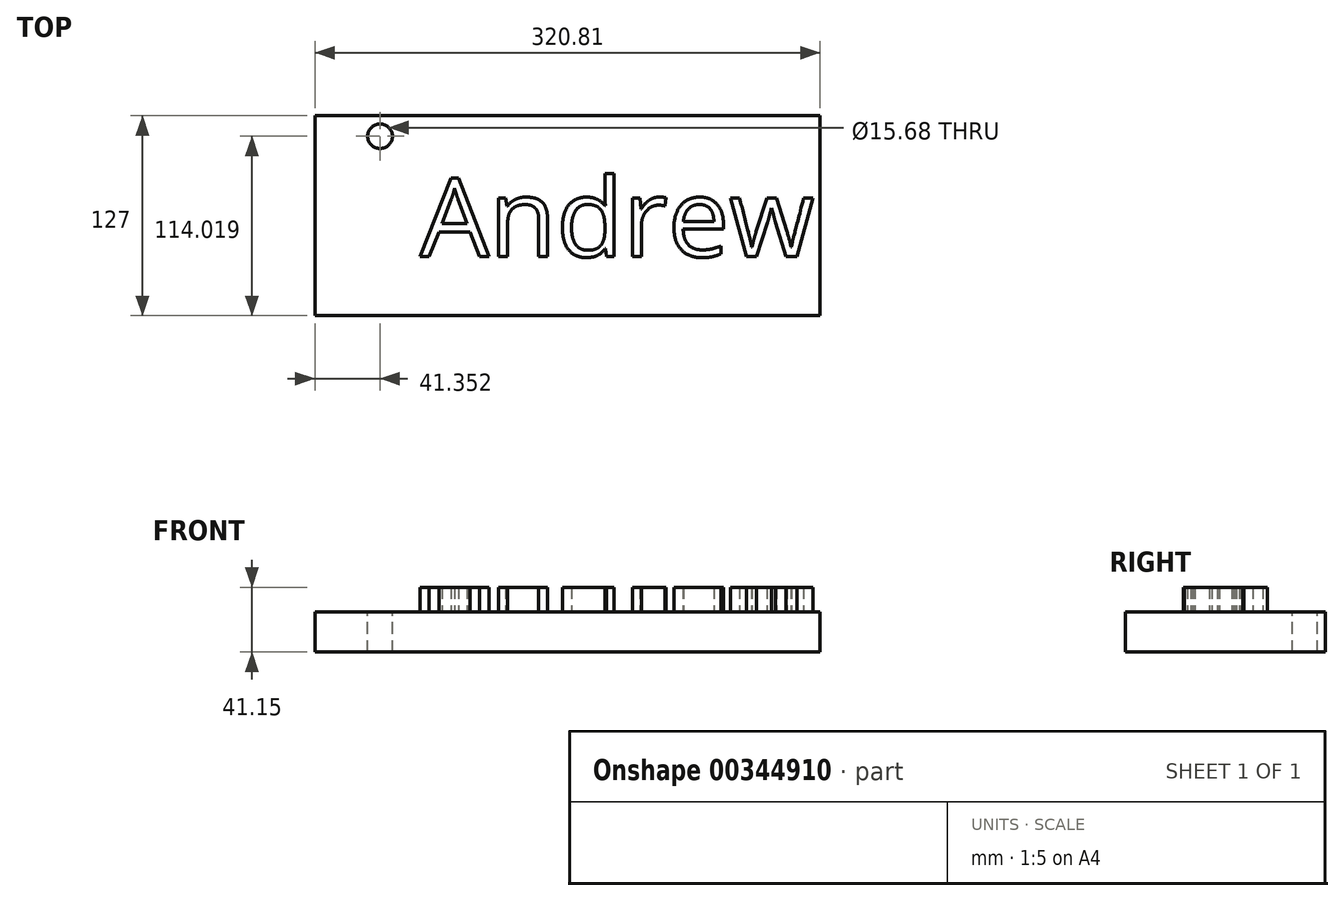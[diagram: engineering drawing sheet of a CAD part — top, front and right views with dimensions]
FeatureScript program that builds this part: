
annotation { "Feature Type Name" : "Feature", "Feature Type Description" : "" }
export const myFeature = defineFeature(function(context is Context, id is Id, definition is map)
    precondition{}
    {
        {
            var Q0;
            Q0=qCreatedBy(makeId("Top.planeOp"),FACE);
            var sketch = newSketch(context, id + "F0", { "sketchPlane" : qUnion([Q0])});
            skLineSegment(sketch, "E0.bottom", {"start": v(-187.13, 76.34) * mm, "end": v(133.68, 76.34) * mm});
            skLineSegment(sketch, "E0.top", {"start": v(-187.13, -50.66) * mm, "end": v(133.68, -50.66) * mm});
            skLineSegment(sketch, "E0.left", {"start": v(-187.13, 76.34) * mm, "end": v(-187.13, -50.66) * mm});
            skLineSegment(sketch, "E0.right", {"start": v(133.68, 76.34) * mm, "end": v(133.68, -50.66) * mm});
            skSolve(sketch);
        }
        {
            var Q0;
            Q0=makeQuery(id+"F0.imprint","IMPRINT",FACE,{"disambiguationData":[TD([[makeQuery(id+"F0.imprint","IMPRINT",EDGE,{"derivedFrom":sQuery(id+"F0.wireOp",EDGE,"E0.bottom")}),-1.0]])]});
            var sketch = newSketch(context, id + "F1", { "sketchPlane" : qUnion([Q0])});
            skText(sketch, "E1", { "text": "Andrew", "fontName": "OpenSans-Regular.ttf"});
            const initialGuessF1  = {"E1": [-0.12038, -0.0131, 1, 0, 0.04996]};
            skSetInitialGuess(sketch, initialGuessF1);
            skSolve(sketch);
        }
        {
            var Q0;
            Q0=makeQuery(id+"F0.imprint","IMPRINT",FACE,{"disambiguationData":[TD([[makeQuery(id+"F0.imprint","IMPRINT",EDGE,{"derivedFrom":sQuery(id+"F0.wireOp",EDGE,"E0.bottom")}),-1.0]])]});
            extrude(context, id + "F2", {"entities" : qUnion([Q0]), "depth" : 25.4 * mm});
        }
        {
            var Q0;
            Q0 = qSketchRegion(id + "F1", true);
            extrude(context, id + "F3", {"entities" : qUnion([Q0]), "operationType" : NewBodyOperationType.ADD, "depth" : 41.15 * mm});
        }
        {
            var Q0;
            {var subQ0=sQuery(id+"F0.wireOp",EDGE,"E0.right");var subQ1=sQuery(id+"F0.wireOp",EDGE,"E0.left");var subQ2=sQuery(id+"F0.wireOp",EDGE,"E0.bottom");var subQ3=sQuery(id+"F0.wireOp",EDGE,"E0.top");Q0=makeQuery(id+"F3.boolean.opBoolean","SPLIT",FACE,{"disambiguationData":[TD([makeQuery(id+"F2.opExtrude","SWEPT_FACE",FACE,{"disambiguationData":[OSD([subQ2])]})])],"derivedFrom":makeQuery(id+"F2.opExtrude","CAP_FACE",FACE,{"disambiguationData":[OSD([subQ2,subQ3,subQ1,subQ0])],"isStart":false})});}
            var sketch = newSketch(context, id + "F4", { "sketchPlane" : qUnion([Q0])});
            skCircle(sketch, "E2", {"center": v(-145.78, 63.36) * mm, "radius": 7.84 * mm});
            skSolve(sketch);
        }
        {
            var Q0;
            Q0=makeQuery(id+"F4.imprint","IMPRINT",FACE,{"disambiguationData":[TD([[makeQuery(id+"F4.imprint","IMPRINT",EDGE,{"derivedFrom":sQuery(id+"F4.wireOp",EDGE,"E2")}),1.0]])]});
            extrude(context, id + "F5", {"entities" : qUnion([Q0]), "operationType" : NewBodyOperationType.REMOVE, "oppositeDirection" : true, "depth" : 156.72 * mm});
        }
    });
